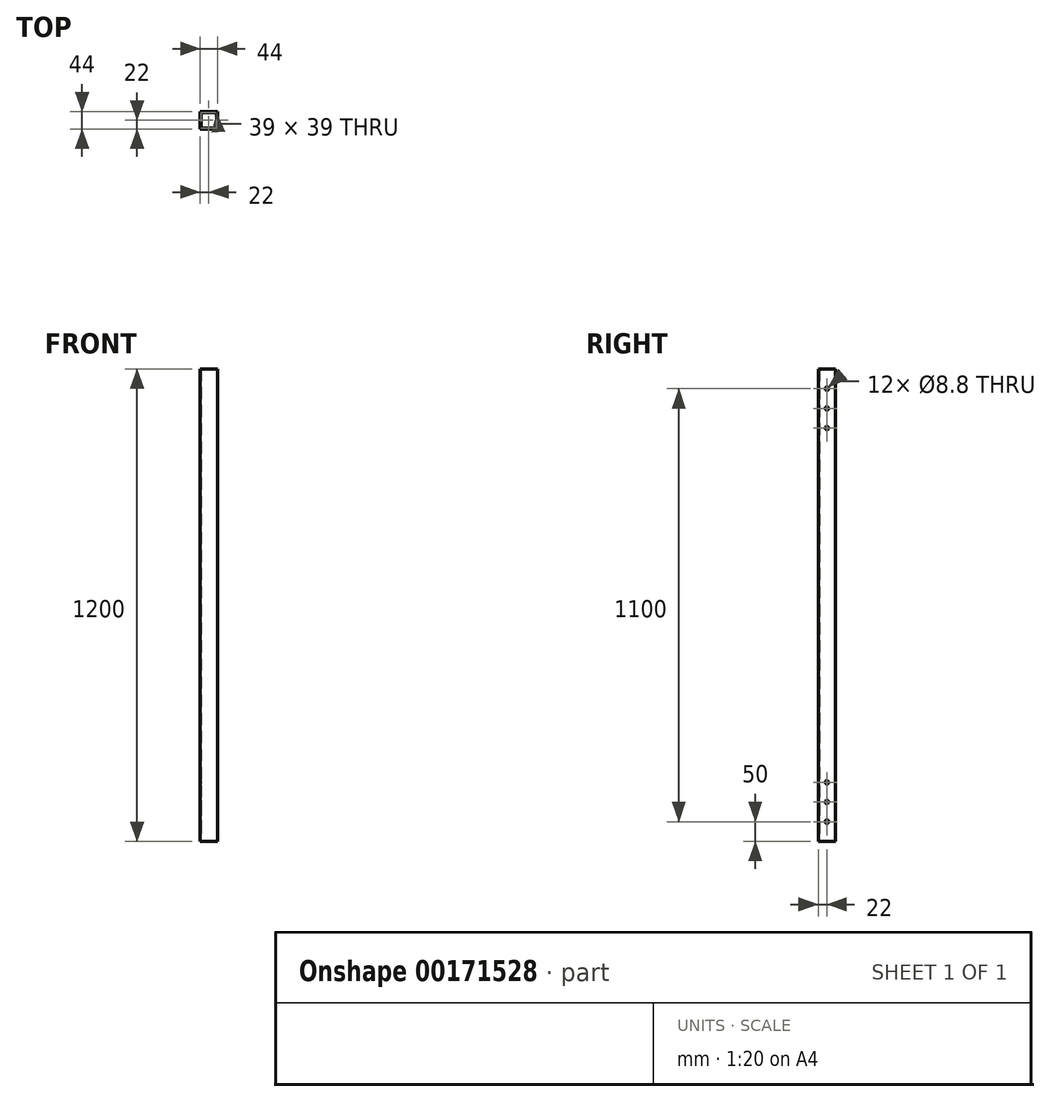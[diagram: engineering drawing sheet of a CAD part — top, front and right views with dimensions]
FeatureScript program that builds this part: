
annotation { "Feature Type Name" : "Feature", "Feature Type Description" : "" }
export const myFeature = defineFeature(function(context is Context, id is Id, definition is map)
    precondition{}
    {
        {
            var Q0;
            Q0=qCreatedBy(makeId("Top.planeOp"),FACE);
            var sketch = newSketch(context, id + "F0", { "sketchPlane" : qUnion([Q0])});
            skLineSegment(sketch, "E0.bottom", {"start": v(22, -22) * mm, "end": v(-22, -22) * mm});
            skLineSegment(sketch, "E0.top", {"start": v(22, 22) * mm, "end": v(-22, 22) * mm});
            skLineSegment(sketch, "E0.left", {"start": v(22, -22) * mm, "end": v(22, 22) * mm});
            skLineSegment(sketch, "E0.right", {"start": v(-22, -22) * mm, "end": v(-22, 22) * mm});
            skPoint(sketch, "E0.middle", {"position": v(0, 0) * mm});
            skLineSegment(sketch, "E1.bottom", {"start": v(19.5, -19.5) * mm, "end": v(-19.5, -19.5) * mm});
            skLineSegment(sketch, "E1.top", {"start": v(19.5, 19.5) * mm, "end": v(-19.5, 19.5) * mm});
            skLineSegment(sketch, "E1.left", {"start": v(19.5, -19.5) * mm, "end": v(19.5, 19.5) * mm});
            skLineSegment(sketch, "E1.right", {"start": v(-19.5, -19.5) * mm, "end": v(-19.5, 19.5) * mm});
            skSolve(sketch);
        }
        {
            var Q0;
            Q0=makeQuery(id+"F0.imprint","IMPRINT",FACE,{"disambiguationData":[TD([[makeQuery(id+"F0.imprint","IMPRINT",EDGE,{"derivedFrom":sQuery(id+"F0.wireOp",EDGE,"E0.bottom")}),-1.0]])]});
            extrude(context, id + "F1", {"entities" : qUnion([Q0]), "depth" : 1200 * mm});
        }
        {
            var Q0;
            Q0=makeQuery(id+"F1.opExtrude","SWEPT_FACE",FACE,{"disambiguationData":[OSD([sQuery(id+"F0.wireOp",EDGE,"E0.right")])]});
            var sketch = newSketch(context, id + "F2", { "sketchPlane" : qUnion([Q0])});
            skPoint(sketch, "E2", {"position": v(0, 1150) * mm});
            skPoint(sketch, "E2.positionSnap0", {"position": v(0, 1200) * mm});
            skPoint(sketch, "E3", {"position": v(0, 1100) * mm});
            skPoint(sketch, "E4", {"position": v(0, 1050) * mm});
            skPoint(sketch, "E5", {"position": v(0, 50) * mm});
            skPoint(sketch, "E5.positionSnap0", {"position": v(0, 0) * mm});
            skPoint(sketch, "E6", {"position": v(0, 100) * mm});
            skPoint(sketch, "E7", {"position": v(0, 150) * mm});
            skSolve(sketch);
        }
        {
            var Q0;
            Q0=sQuery(id+"F2.wireOp",VERTEX,"400cd733-80a3-44c6-8e5b-e4f71ab746b6");
            var Q1;
            Q1=sQuery(id+"F2.wireOp",VERTEX,"666f124d-08e7-4cd1-b467-d99cd41cb88f");
            var Q2;
            Q2=sQuery(id+"F2.wireOp",VERTEX,"3a9d692b-7c3c-444c-8539-e8af0c61a629");
            var Q3;
            Q3=sQuery(id+"F2.wireOp",VERTEX,"E7");
            var Q4;
            Q4=sQuery(id+"F2.wireOp",VERTEX,"E6");
            var Q5;
            Q5=sQuery(id+"F2.wireOp",VERTEX,"E5");
            var Q6;
            Q6=sQuery(id+"F2.wireOp",VERTEX,"E4");
            var Q7;
            Q7=sQuery(id+"F2.wireOp",VERTEX,"E2");
            var Q8;
            Q8=sQuery(id+"F2.wireOp",VERTEX,"E3");
            var Q9;
            Q9=makeQuery(id+"F1.opExtrude","SWEPT_BODY",BODY,{"disambiguationData":[OSD([sQuery(id+"F0.wireOp",EDGE,"E0.bottom"),sQuery(id+"F0.wireOp",EDGE,"E0.top"),sQuery(id+"F0.wireOp",EDGE,"E0.left"),sQuery(id+"F0.wireOp",EDGE,"E0.right"),sQuery(id+"F0.wireOp",EDGE,"E1.bottom"),sQuery(id+"F0.wireOp",EDGE,"E1.top"),sQuery(id+"F0.wireOp",EDGE,"E1.left"),sQuery(id+"F0.wireOp",EDGE,"E1.right")])]});
            hole(context, id + "F3", {"style" : HoleStyle.SIMPLE, "endStyle" : HoleEndStyle.THROUGH, "standardTappedOrClearance" : lookupTablePath({ "standard" : "ISO", "fit" : "Normal", "size" : "M8", "type" : "Clearance" }), "standardBlindInLast" : lookupTablePath({ "fit" : "Standard", "standard" : "ISO", "size" : "M8", "type" : "Clearance" }), "holeDiameter" : 8.8 * mm, "locations" : qUnion([Q0, Q1, Q2, Q3, Q4, Q5, Q6, Q7, Q8]), "scope" : qUnion([Q9]), "isTappedThrough" : true});
        }
    });
